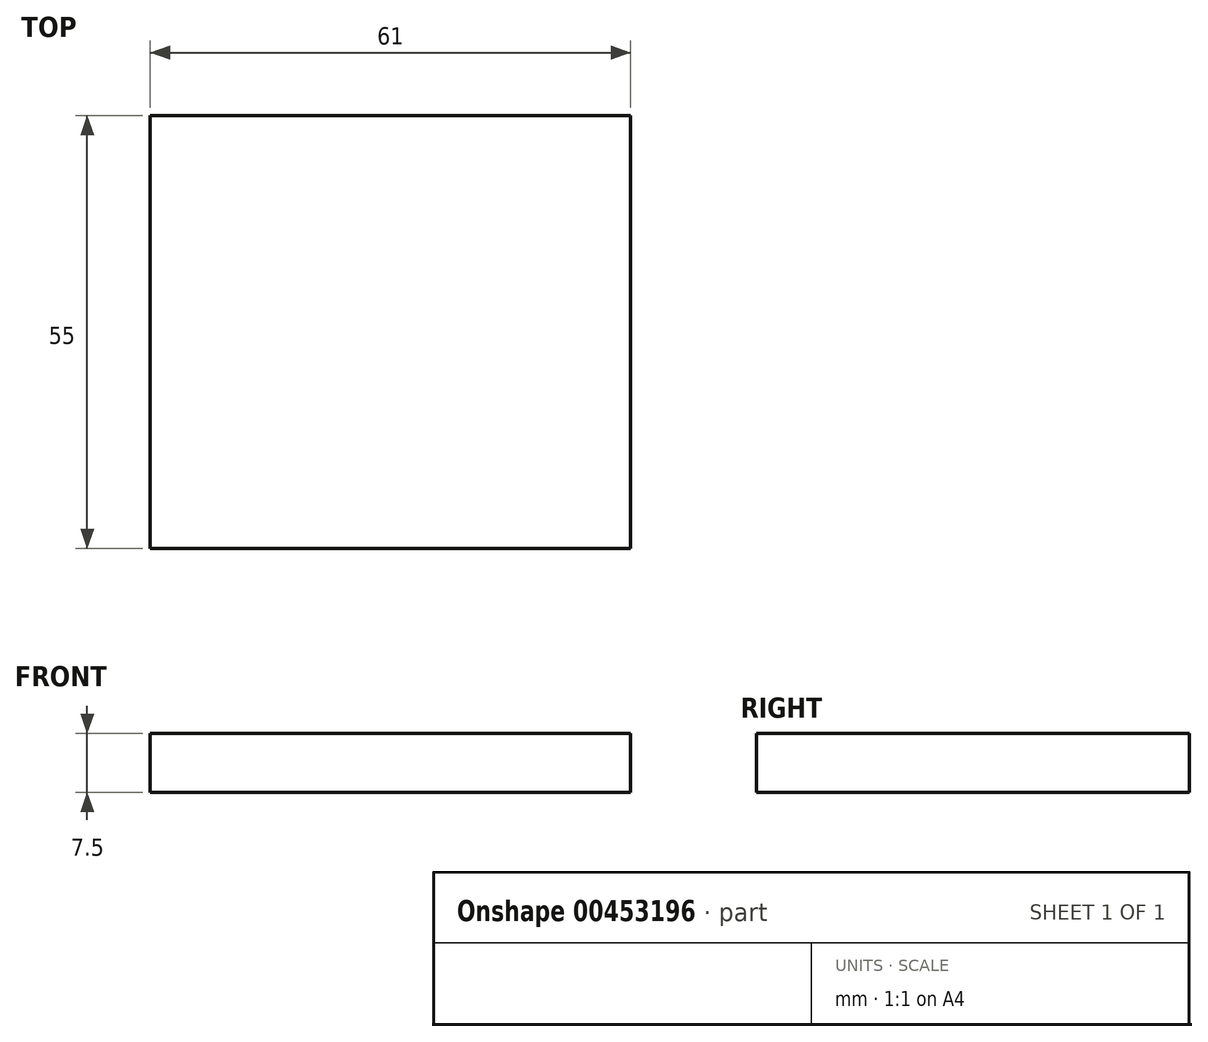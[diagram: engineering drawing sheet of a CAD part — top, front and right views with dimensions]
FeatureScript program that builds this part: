
annotation { "Feature Type Name" : "Feature", "Feature Type Description" : "" }
export const myFeature = defineFeature(function(context is Context, id is Id, definition is map)
    precondition{}
    {
        {
            var Q0;
            Q0=qCreatedBy(makeId("Top.planeOp"),FACE);
            var sketch = newSketch(context, id + "F0", { "sketchPlane" : qUnion([Q0])});
            skLineSegment(sketch, "E0.bottom", {"start": v(0, 0) * mm, "end": v(-61, 0) * mm});
            skLineSegment(sketch, "E0.top", {"start": v(0, -55) * mm, "end": v(-61, -55) * mm});
            skLineSegment(sketch, "E0.left", {"start": v(0, 0) * mm, "end": v(0, -55) * mm});
            skLineSegment(sketch, "E0.right", {"start": v(-61, 0) * mm, "end": v(-61, -55) * mm});
            skSolve(sketch);
        }
        {
            var Q0;
            Q0=qSketchRegion(id+"F0",true);
            extrude(context, id + "F1", {"entities" : qUnion([Q0]), "depth" : 7.5 * mm});
        }
    });
